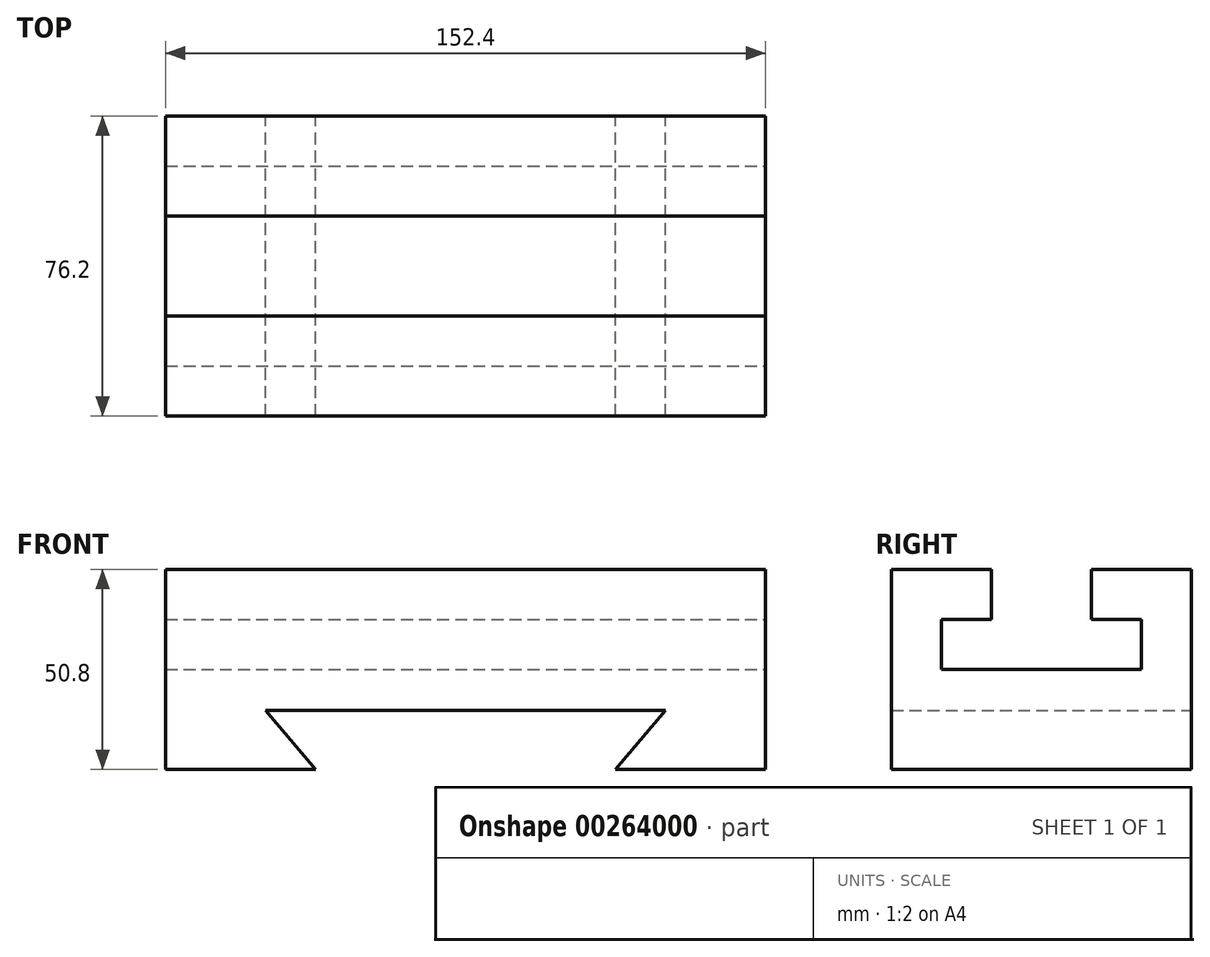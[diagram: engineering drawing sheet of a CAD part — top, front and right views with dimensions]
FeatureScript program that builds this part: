
annotation { "Feature Type Name" : "Feature", "Feature Type Description" : "" }
export const myFeature = defineFeature(function(context is Context, id is Id, definition is map)
    precondition{}
    {
        {
            var Q0;
            Q0=qCreatedBy(makeId("Front.planeOp"),FACE);
            var sketch = newSketch(context, id + "F0", { "sketchPlane" : qUnion([Q0])});
            skLineSegment(sketch, "E0", {"start": v(-76.56, 50.8) * mm, "end": v(-76.56, 0) * mm});
            skLineSegment(sketch, "E1", {"start": v(-76.56, 50.8) * mm, "end": v(75.84, 50.8) * mm});
            skLineSegment(sketch, "E2", {"start": v(-76.56, 0) * mm, "end": v(-38.46, 0) * mm});
            skLineSegment(sketch, "E3", {"start": v(75.84, 0) * mm, "end": v(71.95, 0) * mm});
            skLineSegment(sketch, "E4", {"start": v(75.84, 50.8) * mm, "end": v(75.84, 0) * mm});
            skLineSegment(sketch, "E5", {"start": v(75.84, 0) * mm, "end": v(37.74, 0) * mm});
            skLineSegment(sketch, "E6", {"start": v(37.74, 0) * mm, "end": v(50.44, 14.97) * mm});
            skLineSegment(sketch, "E7", {"start": v(50.44, 14.97) * mm, "end": v(-51.16, 14.97) * mm});
            skLineSegment(sketch, "E8", {"start": v(-51.16, 14.97) * mm, "end": v(-38.46, 0) * mm});
            skSolve(sketch);
        }
        {
            var Q0;
            Q0=makeQuery(id+"F0.imprint","IMPRINT",FACE,{"disambiguationData":[TD([[makeQuery(id+"F0.imprint","IMPRINT",EDGE,{"derivedFrom":sQuery(id+"F0.wireOp",EDGE,"E0")}),1.0]])]});
            extrude(context, id + "F1", {"entities" : qUnion([Q0]), "depth" : 76.2 * mm});
        }
        {
            var Q0;
            Q0=makeQuery(id+"F1.opExtrude","SWEPT_FACE",FACE,{"disambiguationData":[OSD([sQuery(id+"F0.wireOp",EDGE,"E4")])]});
            var sketch = newSketch(context, id + "F2", { "sketchPlane" : qUnion([Q0])});
            skLineSegment(sketch, "E9", {"start": v(-76.2, 50.8) * mm, "end": v(-50.8, 50.8) * mm});
            skLineSegment(sketch, "E10", {"start": v(-50.8, 50.8) * mm, "end": v(-50.8, 38.1) * mm});
            skLineSegment(sketch, "E11", {"start": v(-50.8, 38.1) * mm, "end": v(-63.5, 38.1) * mm});
            skLineSegment(sketch, "E12", {"start": v(-63.5, 38.1) * mm, "end": v(-63.5, 25.4) * mm});
            skLineSegment(sketch, "E13", {"start": v(-63.5, 25.4) * mm, "end": v(-12.7, 25.4) * mm});
            skLineSegment(sketch, "E14", {"start": v(-12.7, 25.4) * mm, "end": v(-12.7, 38.1) * mm});
            skLineSegment(sketch, "E15", {"start": v(-12.7, 38.1) * mm, "end": v(-25.4, 38.1) * mm});
            skLineSegment(sketch, "E16", {"start": v(-25.4, 38.1) * mm, "end": v(-25.4, 50.8) * mm});
            skSolve(sketch);
        }
        {
            var Q0;
            {var subQ0=sQuery(id+"F2.wireOp",EDGE,"E10");Q0=makeQuery(id+"F2.imprint","IMPRINT",FACE,{"disambiguationData":[TD([[makeQuery(id+"F2.imprint","IMPRINT",EDGE,{"derivedFrom":subQ0}),1.0]])]});}
            extrude(context, id + "F3", {"entities" : qUnion([Q0]), "operationType" : NewBodyOperationType.REMOVE, "oppositeDirection" : true, "depth" : 152.4 * mm});
        }
    });
